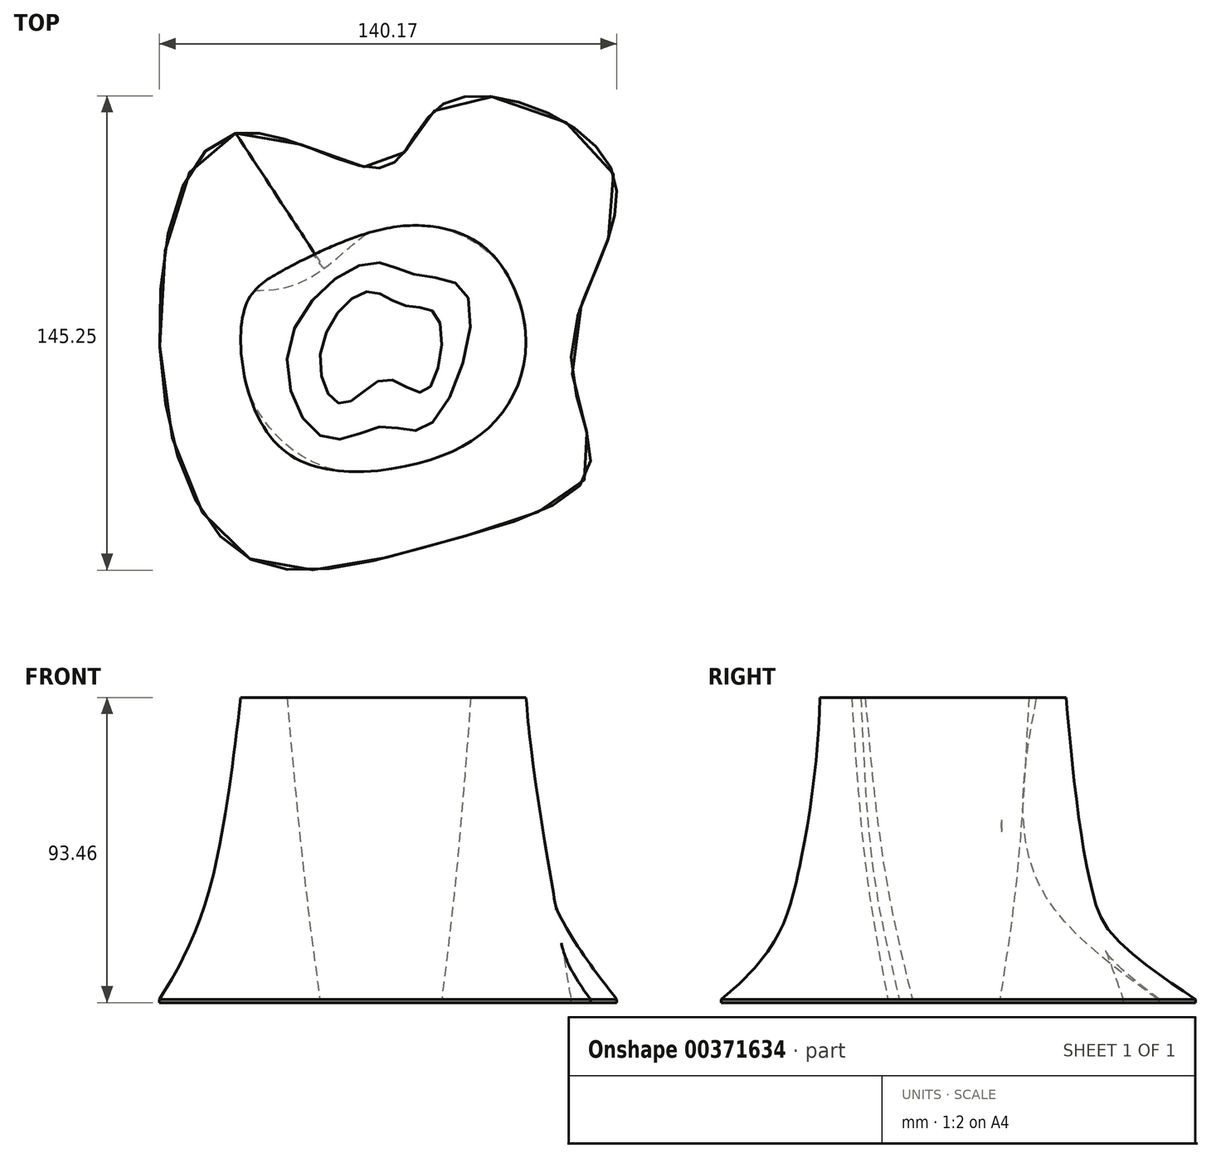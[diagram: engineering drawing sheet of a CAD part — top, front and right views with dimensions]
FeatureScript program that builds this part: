
annotation { "Feature Type Name" : "Feature", "Feature Type Description" : "" }
export const myFeature = defineFeature(function(context is Context, id is Id, definition is map)
    precondition{}
    {
        {
            var Q0;
            Q0=qCreatedBy(makeId("Top.planeOp"),FACE);
            var sketch = newSketch(context, id + "F0", { "sketchPlane" : qUnion([Q0])});
            skFitSpline(sketch, "E0", {"points": [v(-111.86, 42.17) * mm, v(-135.28, -19.94) * mm, v(-108.82, -87.42) * mm, v(-49.57, -83.34) * mm, v(-3.9, -61.4) * mm, v(-9.1, -23.14) * mm, v(3.42, 30.8) * mm, v(-46.75, 52) * mm, v(-66.04, 31.92) * mm, v(-111.86, 42.17) * mm]});
            skSolve(sketch);
        }
        {
            var Q0;
            Q0=qCreatedBy(makeId("Top.planeOp"),FACE);
            cPlane(context, id + "F1", {"entities" : qUnion([Q0]), "cplaneType" : CPlaneType.OFFSET, "offset" : 92.46 * mm, "width" : 152.4 * mm, "height" : 152.4 * mm});
        }
        {
            var Q0;
            Q0=qCreatedBy(id+"F1.planeOp",FACE);
            var sketch = newSketch(context, id + "F2", { "sketchPlane" : qUnion([Q0])});
            skFitSpline(sketch, "E1", {"points": [v(-32.09, 3.77) * mm, v(-47.5, 12.9) * mm, v(-68.45, 12.5) * mm, v(-97.83, 0) * mm, v(-109.47, -12.58) * mm, v(-98.81, -53.44) * mm, v(-58.6, -59.49) * mm, v(-32.4, -45.93) * mm, v(-22.96, -22.02) * mm, v(-32.09, 3.77) * mm]});
            skSolve(sketch);
        }
        {
            var Q0;
            Q0=qCreatedBy(makeId("Top.planeOp"),FACE);
            cPlane(context, id + "F3", {"entities" : qUnion([Q0]), "cplaneType" : CPlaneType.OFFSET, "offset" : 30.48 * mm, "width" : 152.4 * mm, "height" : 152.4 * mm});
        }
        {
            var Q0;
            Q0=qCreatedBy(id+"F3.planeOp",FACE);
            var sketch = newSketch(context, id + "F4", { "sketchPlane" : qUnion([Q0])});
            skFitSpline(sketch, "E2", {"points": [v(-71.73, 19.1) * mm, v(-45.66, 21.42) * mm, v(-19.44, 4.92) * mm, v(-14.52, -26.34) * mm, v(-18.69, -55.21) * mm, v(-57.27, -69.92) * mm, v(-104.2, -54.36) * mm, v(-120, -10.22) * mm, v(-103.91, 0) * mm, v(-71.73, 19.1) * mm]});
            skSolve(sketch);
        }
        {
            var Q0;
            Q0=makeQuery(id+"F0.imprint","IMPRINT",FACE,{"disambiguationData":[TD([[makeQuery(id+"F0.imprint","IMPRINT",EDGE,{"derivedFrom":sQuery(id+"F0.wireOp",EDGE,"E0")}),1.0]])]});
            var Q1;
            Q1=makeQuery(id+"F4.imprint","IMPRINT",FACE,{"disambiguationData":[TD([[makeQuery(id+"F4.imprint","IMPRINT",EDGE,{"derivedFrom":sQuery(id+"F4.wireOp",EDGE,"E2")}),-1.0]])]});
            var Q2;
            Q2=makeQuery(id+"F2.imprint","IMPRINT",FACE,{"disambiguationData":[TD([[makeQuery(id+"F2.imprint","IMPRINT",EDGE,{"derivedFrom":sQuery(id+"F2.wireOp",EDGE,"E1")}),1.0]])]});
            loft(context, id + "F5", {"sheetProfilesArray" : [{ "sheetProfileEntities" : qUnion([Q0]) }, { "sheetProfileEntities" : qUnion([Q1]) }, { "sheetProfileEntities" : qUnion([Q2]) }]});
        }
        {
            var Q0;
            Q0=qCreatedBy(makeId("Top.planeOp"),FACE);
            var sketch = newSketch(context, id + "F6", { "sketchPlane" : qUnion([Q0])});
            skFitSpline(sketch, "E3", {"points": [v(21.4, 11.95) * mm, v(7.23, -7.23) * mm, v(14.16, -22.33) * mm, v(27.37, -14.78) * mm, v(39.32, -18.56) * mm, v(43.1, 4.4) * mm, v(32.71, 7.86) * mm, v(21.4, 11.95) * mm]});
            skSolve(sketch);
        }
        {
            var Q0;
            Q0=qCreatedBy(id+"F3.planeOp",FACE);
            var sketch = newSketch(context, id + "F7", { "sketchPlane" : qUnion([Q0])});
            skFitSpline(sketch, "E4", {"points": [v(46.56, 8.18) * mm, v(34.6, 11.64) * mm, v(21.4, 16.36) * mm, v(3.46, -5.66) * mm, v(12.27, -27.68) * mm, v(27.37, -21.7) * mm, v(40.26, -24.85) * mm, v(46.56, 8.18) * mm]});
            skSolve(sketch);
        }
        {
            var Q0;
            Q0=qCreatedBy(id+"F1.planeOp",FACE);
            var sketch = newSketch(context, id + "F8", { "sketchPlane" : qUnion([Q0])});
            skFitSpline(sketch, "E5", {"points": [v(52.22, 11) * mm, v(36.17, 17.3) * mm, v(22.02, 20.76) * mm, v(-2.52, -5.03) * mm, v(9.44, -33.03) * mm, v(26.74, -29.25) * mm, v(40.26, -29.25) * mm, v(52.22, 11) * mm]});
            skSolve(sketch);
        }
        {
            var Q0;
            Q0=makeQuery(id+"F6.imprint","IMPRINT",FACE,{"disambiguationData":[TD([[makeQuery(id+"F6.imprint","IMPRINT",EDGE,{"derivedFrom":sQuery(id+"F6.wireOp",EDGE,"E3")}),1.0]])]});
            var Q1;
            Q1=makeQuery(id+"F7.imprint","IMPRINT",FACE,{"disambiguationData":[TD([[makeQuery(id+"F7.imprint","IMPRINT",EDGE,{"derivedFrom":sQuery(id+"F7.wireOp",EDGE,"E4")}),1.0]])]});
            var Q2;
            Q2=makeQuery(id+"F8.imprint","IMPRINT",FACE,{"disambiguationData":[TD([[makeQuery(id+"F8.imprint","IMPRINT",EDGE,{"derivedFrom":sQuery(id+"F8.wireOp",EDGE,"E5")}),1.0]])]});
            loft(context, id + "F9", {"sheetProfilesArray" : [{ "sheetProfileEntities" : qUnion([Q0]) }, { "sheetProfileEntities" : qUnion([Q1]) }, { "sheetProfileEntities" : qUnion([Q2]) }]});
        }
        {
            var Q0;
            Q0=makeQuery(id+"F9.opLoft","SWEPT_BODY",BODY,{"disambiguationData":[OSD([makeQuery(id+"F6.imprint","IMPRINT",FACE,{"disambiguationData":[TD([[makeQuery(id+"F6.imprint","IMPRINT",EDGE,{"derivedFrom":sQuery(id+"F6.wireOp",EDGE,"E3")}),1.0]])]}),sQuery(id+"F7.wireOp",EDGE,"E4"),makeQuery(id+"F8.imprint","IMPRINT",FACE,{"disambiguationData":[TD([[makeQuery(id+"F8.imprint","IMPRINT",EDGE,{"derivedFrom":sQuery(id+"F8.wireOp",EDGE,"E5")}),1.0]])]})])]});
            var Q1;
            Q1=qCreatedBy(makeId("Right.planeOp"),FACE);
            transform(context, id + "F10", {"entities" : qUnion([Q0]), "transformType" : TransformType.TRANSLATION_DISTANCE, "transformDirection" : qUnion([Q1]), "distance" : 93.22 * mm, "oppositeDirection" : true, "makeCopy" : false});
        }
        {
            var Q0;
            Q0=makeQuery(id+"F9.opLoft","SWEPT_BODY",BODY,{"disambiguationData":[OSD([makeQuery(id+"F6.imprint","IMPRINT",FACE,{"disambiguationData":[TD([[makeQuery(id+"F6.imprint","IMPRINT",EDGE,{"derivedFrom":sQuery(id+"F6.wireOp",EDGE,"E3")}),1.0]])]}),sQuery(id+"F7.wireOp",EDGE,"E4"),makeQuery(id+"F8.imprint","IMPRINT",FACE,{"disambiguationData":[TD([[makeQuery(id+"F8.imprint","IMPRINT",EDGE,{"derivedFrom":sQuery(id+"F8.wireOp",EDGE,"E5")}),1.0]])]})])]});
            var Q1;
            Q1=qCreatedBy(makeId("Front.planeOp"),FACE);
            transform(context, id + "F11", {"entities" : qUnion([Q0]), "transformType" : TransformType.TRANSLATION_DISTANCE, "transformDirection" : qUnion([Q1]), "distance" : 18.29 * mm, "makeCopy" : false});
        }
        {
            var Q0;
            Q0=makeQuery(id+"F5.opLoft","CAP_FACE",FACE,{"disambiguationData":[OSD([makeQuery(id+"F0.imprint","IMPRINT",FACE,{"disambiguationData":[TD([[makeQuery(id+"F0.imprint","IMPRINT",EDGE,{"derivedFrom":sQuery(id+"F0.wireOp",EDGE,"E0")}),1.0]])]})])],"isStart":true});
            extrude(context, id + "F12", {"entities" : qUnion([Q0]), "depth" : 1 * mm});
        }
        {
            var Q0;
            Q0=makeQuery(id+"F9.opLoft","SWEPT_BODY",BODY,{"disambiguationData":[OSD([makeQuery(id+"F6.imprint","IMPRINT",FACE,{"disambiguationData":[TD([[makeQuery(id+"F6.imprint","IMPRINT",EDGE,{"derivedFrom":sQuery(id+"F6.wireOp",EDGE,"E3")}),1.0]])]}),sQuery(id+"F7.wireOp",EDGE,"E4"),makeQuery(id+"F8.imprint","IMPRINT",FACE,{"disambiguationData":[TD([[makeQuery(id+"F8.imprint","IMPRINT",EDGE,{"derivedFrom":sQuery(id+"F8.wireOp",EDGE,"E5")}),1.0]])]})])]});
            var Q1;
            Q1=makeQuery(id+"F5.opLoft","SWEPT_BODY",BODY,{"disambiguationData":[OSD([makeQuery(id+"F0.imprint","IMPRINT",FACE,{"disambiguationData":[TD([[makeQuery(id+"F0.imprint","IMPRINT",EDGE,{"derivedFrom":sQuery(id+"F0.wireOp",EDGE,"E0")}),1.0]])]}),makeQuery(id+"F2.imprint","IMPRINT",FACE,{"disambiguationData":[TD([[makeQuery(id+"F2.imprint","IMPRINT",EDGE,{"derivedFrom":sQuery(id+"F2.wireOp",EDGE,"E1")}),1.0]])]}),sQuery(id+"F4.wireOp",EDGE,"E2")])]});
            booleanBodies(context, id + "F13", {"operationType" : BooleanOperationType.SUBTRACTION, "tools" : qUnion([Q0]), "targets" : qUnion([Q1])});
        }
        {
            var Q0;
            Q0=qCreatedBy(makeId("Top.planeOp"),FACE);
            cPlane(context, id + "F14", {"entities" : qUnion([Q0]), "cplaneType" : CPlaneType.OFFSET, "offset" : 163 * mm, "width" : 152.4 * mm, "height" : 152.4 * mm});
        }
    });
